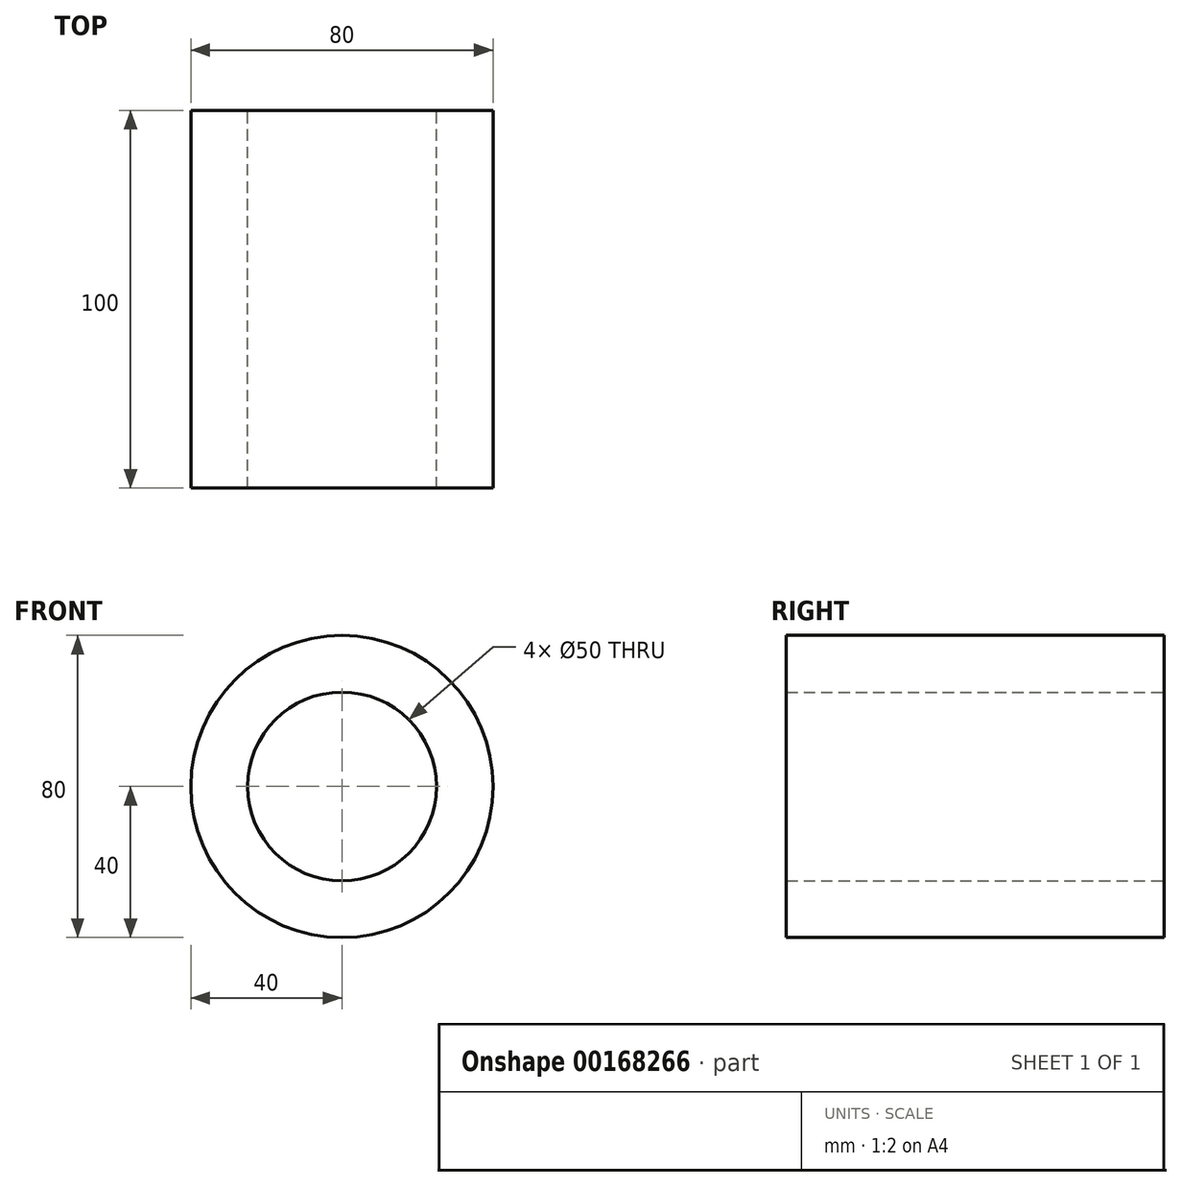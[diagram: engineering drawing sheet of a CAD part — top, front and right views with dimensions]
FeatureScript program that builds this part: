
annotation { "Feature Type Name" : "Feature", "Feature Type Description" : "" }
export const myFeature = defineFeature(function(context is Context, id is Id, definition is map)
    precondition{}
    {
        {
            var Q0;
            Q0=qCreatedBy(makeId("Front.planeOp"),FACE);
            var sketch = newSketch(context, id + "F0", { "sketchPlane" : qUnion([Q0])});
            skCircle(sketch, "E0", {"center": v(0, 0) * mm, "radius": 40 * mm});
            skCircle(sketch, "E1", {"center": v(0, 0) * mm, "radius": 25 * mm});
            skSolve(sketch);
        }
        {
            var Q0;
            Q0=makeQuery(id+"F0.imprint","IMPRINT",FACE,{"disambiguationData":[TD([[makeQuery(id+"F0.imprint","IMPRINT",EDGE,{"derivedFrom":sQuery(id+"F0.wireOp",EDGE,"E0")}),1.0]])]});
            extrude(context, id + "F1", {"entities" : qUnion([Q0]), "depth" : 100 * mm});
        }
    });
